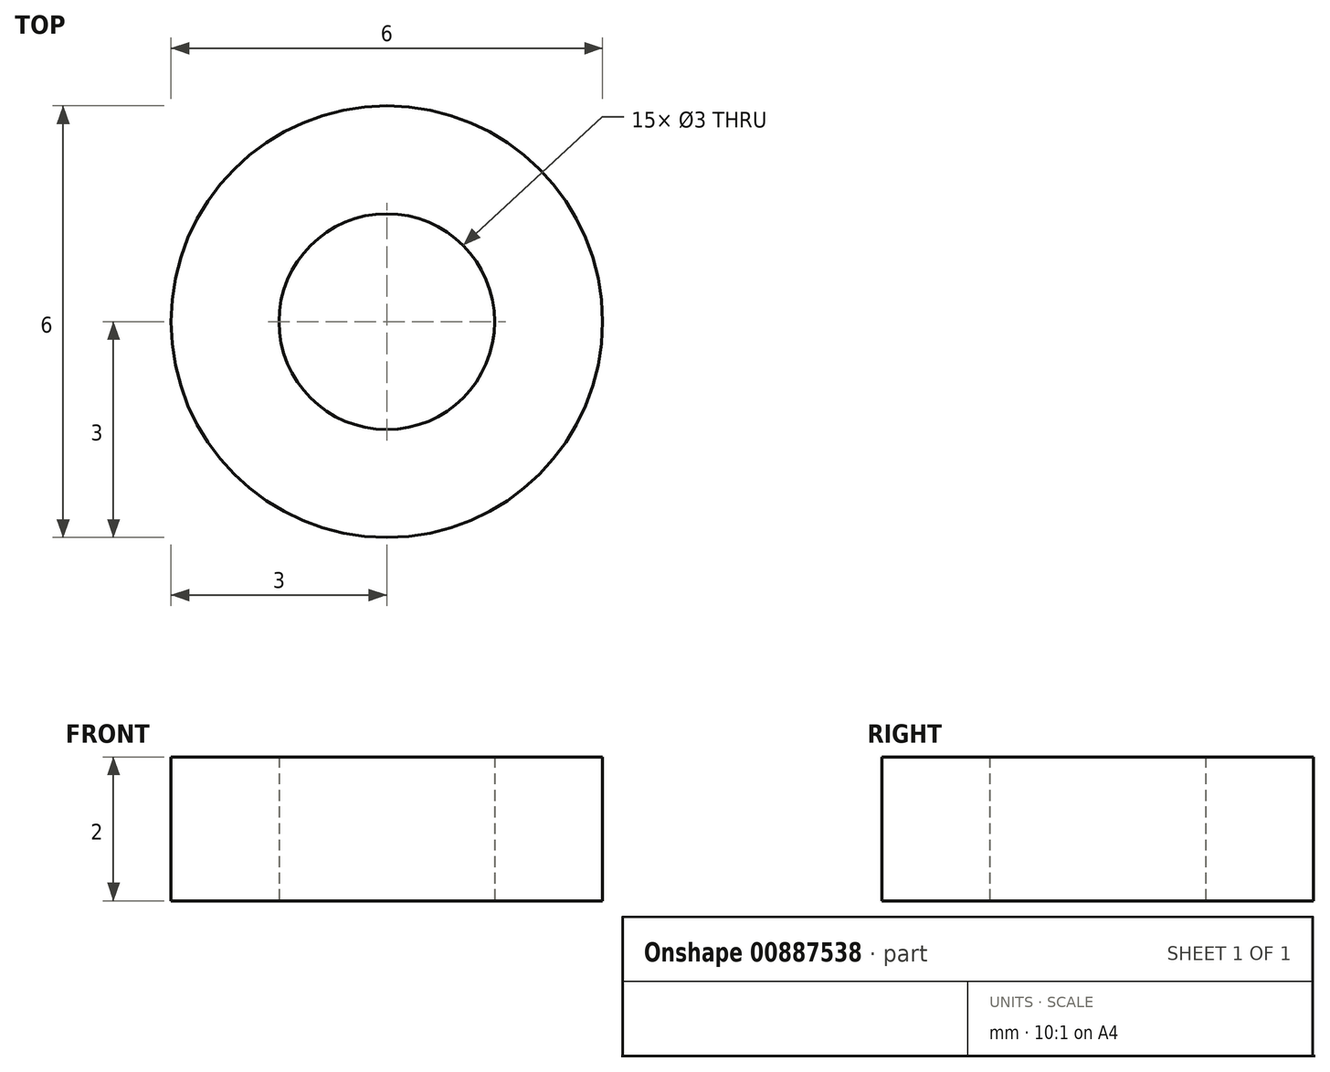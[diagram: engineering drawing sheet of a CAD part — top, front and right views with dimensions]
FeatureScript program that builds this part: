
annotation { "Feature Type Name" : "Feature", "Feature Type Description" : "" }
export const myFeature = defineFeature(function(context is Context, id is Id, definition is map)
    precondition{}
    {
        {
            var Q0;
            Q0=qCreatedBy(makeId("Top.planeOp"),FACE);
            var sketch = newSketch(context, id + "F0", { "sketchPlane" : qUnion([Q0])});
            skCircle(sketch, "E0", {"center": v(0, 0) * mm, "radius": 3 * mm});
            skCircle(sketch, "E1", {"center": v(0, 0) * mm, "radius": 1.5 * mm});
            skSolve(sketch);
        }
        {
            var Q0;
            Q0=makeQuery(id+"F0.imprint","IMPRINT",FACE,{"disambiguationData":[TD([[makeQuery(id+"F0.imprint","IMPRINT",EDGE,{"derivedFrom":sQuery(id+"F0.wireOp",EDGE,"E0")}),1.0]])]});
            extrude(context, id + "F1", {"entities" : qUnion([Q0]), "depth" : 2 * mm, "offsetDistance" : 25 * mm});
        }
    });
